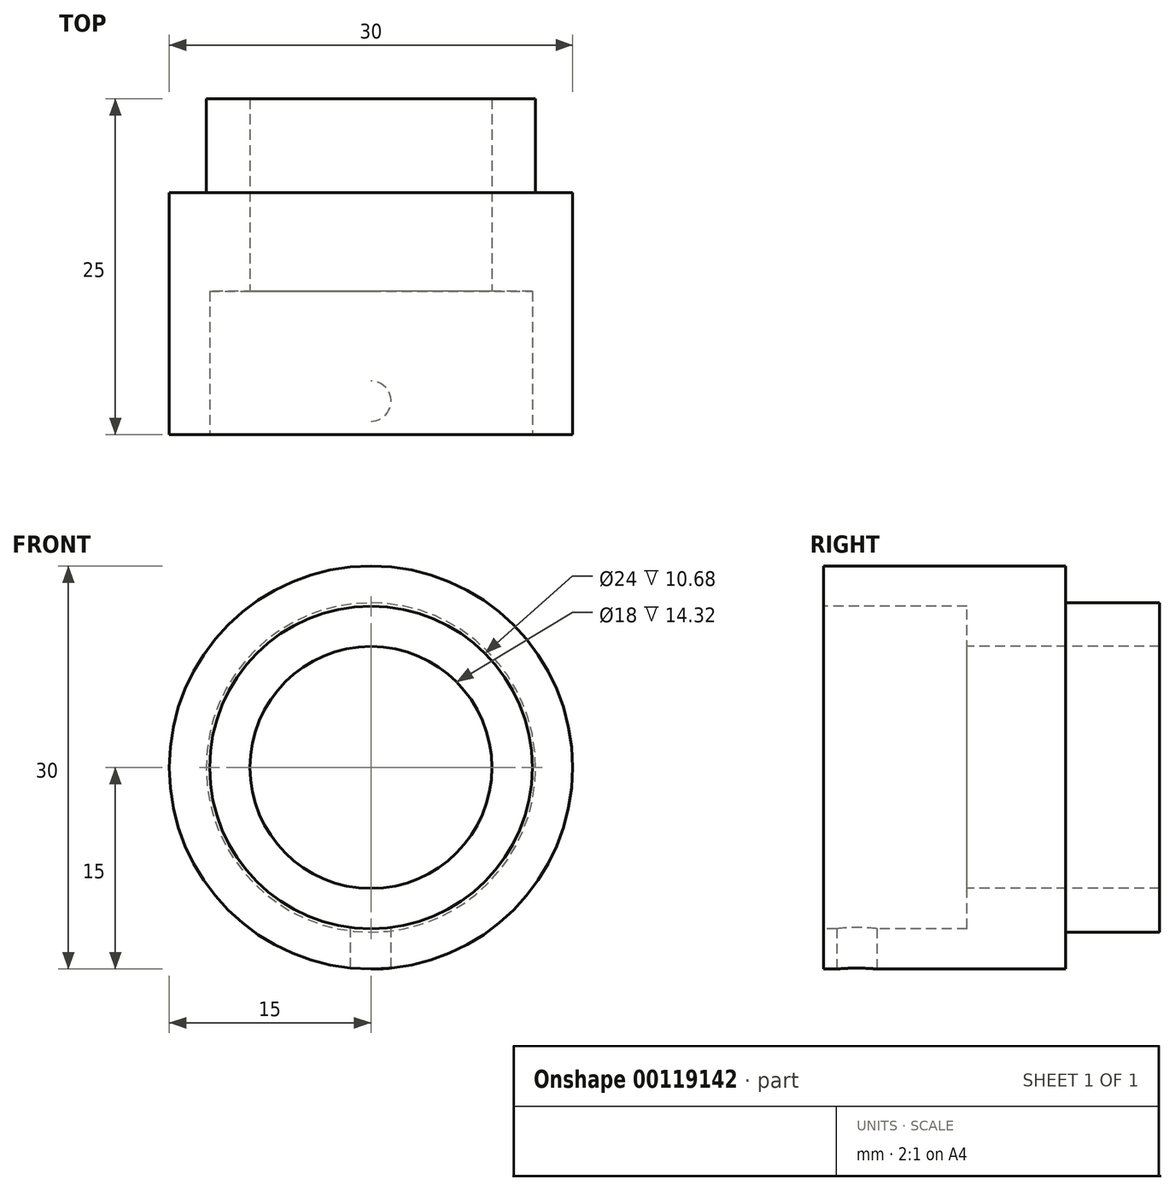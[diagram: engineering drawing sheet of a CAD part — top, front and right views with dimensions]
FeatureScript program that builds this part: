
annotation { "Feature Type Name" : "Feature", "Feature Type Description" : "" }
export const myFeature = defineFeature(function(context is Context, id is Id, definition is map)
    precondition{}
    {
        {
            var Q0;
            Q0=qCreatedBy(makeId("Right.planeOp"),FACE);
            var sketch = newSketch(context, id + "F0", { "sketchPlane" : qUnion([Q0])});
            skLineSegment(sketch, "E0", {"start": v(0, 15) * mm, "end": v(18, 15) * mm});
            skLineSegment(sketch, "E1", {"start": v(18, 15) * mm, "end": v(18, 12.25) * mm});
            skLineSegment(sketch, "E2", {"start": v(18, 12.25) * mm, "end": v(25, 12.25) * mm});
            skLineSegment(sketch, "E3", {"start": v(25, 12.25) * mm, "end": v(25, 9) * mm});
            skLineSegment(sketch, "E4", {"start": v(25, 9) * mm, "end": v(10.68, 9) * mm});
            skLineSegment(sketch, "E5", {"start": v(0, 15) * mm, "end": v(0, 12) * mm});
            skLineSegment(sketch, "E6", {"start": v(0, 0) * mm, "end": v(62.1, 0) * mm});
            skLineSegment(sketch, "E7", {"start": v(0, 12) * mm, "end": v(10.68, 12) * mm});
            skLineSegment(sketch, "E8", {"start": v(10.68, 12) * mm, "end": v(10.68, 9) * mm});
            skPoint(sketch, "E9.orphan", {"position": v(0, 9) * mm});
            skSolve(sketch);
        }
        {
            var Q0;
            Q0=makeQuery(id+"F0.imprint","IMPRINT",FACE,{"disambiguationData":[TD([[makeQuery(id+"F0.imprint","IMPRINT",EDGE,{"derivedFrom":sQuery(id+"F0.wireOp",EDGE,"E0")}),-1.0]])]});
            var Q1;
            Q1=sQuery(id+"F0.wireOp",EDGE,"E6");
            revolve(context, id + "F1", {"entities" : qUnion([Q0]), "axis" : qUnion([Q1]), "revolveType" : RevolveType.FULL});
        }
        {
            var Q0;
            Q0=qCreatedBy(makeId("Top.planeOp"),FACE);
            var sketch = newSketch(context, id + "F2", { "sketchPlane" : qUnion([Q0])});
            skPoint(sketch, "E10", {"position": v(0, 2.5) * mm});
            skPoint(sketch, "E11", {"position": v(0, 0) * mm});
            skSolve(sketch);
        }
        {
            var Q0;
            Q0=sQuery(id+"F2.wireOp",VERTEX,"E10");
            var Q1;
            Q1=makeQuery(id+"F1.opRevolve","SWEPT_BODY",BODY,{"disambiguationData":[OSD([sQuery(id+"F0.wireOp",EDGE,"E0"),sQuery(id+"F0.wireOp",EDGE,"E1"),sQuery(id+"F0.wireOp",EDGE,"E2"),sQuery(id+"F0.wireOp",EDGE,"E3"),sQuery(id+"F0.wireOp",EDGE,"E4"),sQuery(id+"F0.wireOp",EDGE,"E5"),sQuery(id+"F0.wireOp",EDGE,"E7"),sQuery(id+"F0.wireOp",EDGE,"E8")])]});
            hole(context, id + "F3", {"style" : HoleStyle.SIMPLE, "endStyle" : HoleEndStyle.THROUGH, "holeDiameter" : 3 * mm, "locations" : qUnion([Q0]), "scope" : qUnion([Q1]), "isTappedThrough" : true});
        }
    });
